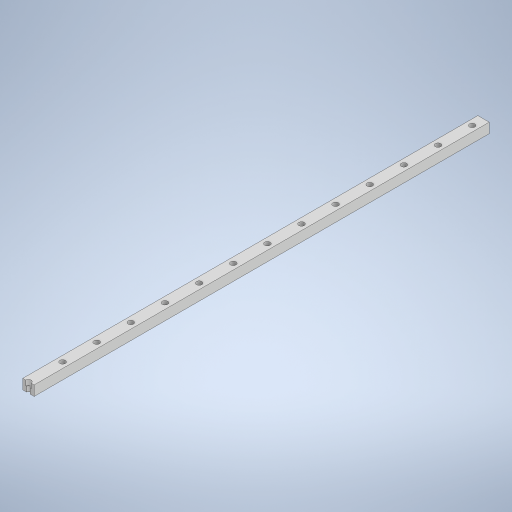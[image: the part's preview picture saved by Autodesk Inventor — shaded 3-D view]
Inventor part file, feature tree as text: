
AUTODESK INVENTOR PART (.ipt)
format: ipt  version: 2023 (Build 270158000, 158)  size: 280,576 bytes
history: native  units: mm
features: extrude x3, sketch x3, pattern_linear x1
ambient origin geometry x8: Origin, YZ Plane, XZ Plane, XY Plane, X Axis, Y Axis, Z Axis, Center Point
bodies: Solid1 (feature_tree)
feature tree (7):
  extrude  "Extrusion1"  Depth=17.5mm
  extrude  "Extrusion2"  Depth=800.0mm
  extrude  "Extrusion3"  Depth=800.0mm TaperAngle=0.0deg
  pattern_linear  "Rectangular Pattern1"  Spacing1=9.5mm  [1 undecoded]
  sketch  "Sketch1"  dims[d0=20.0mm d1=17.5mm]
  sketch  "Sketch2"  dims[d2=800.0mm d3=0.0mm d4=6.0mm]
  sketch  "Sketch3"  dims[d5=20.0mm d6=800.0mm d7=0.0mm d8=9.5mm d9=8.5mm d10=0.0mm d11=180.0mm d13=60.0mm]
note: 1 required parameter value undecoded (feature->parameter linkage not recoverable at this tier; creation-order binding heuristic only, values carry confidence <= 0.55)
